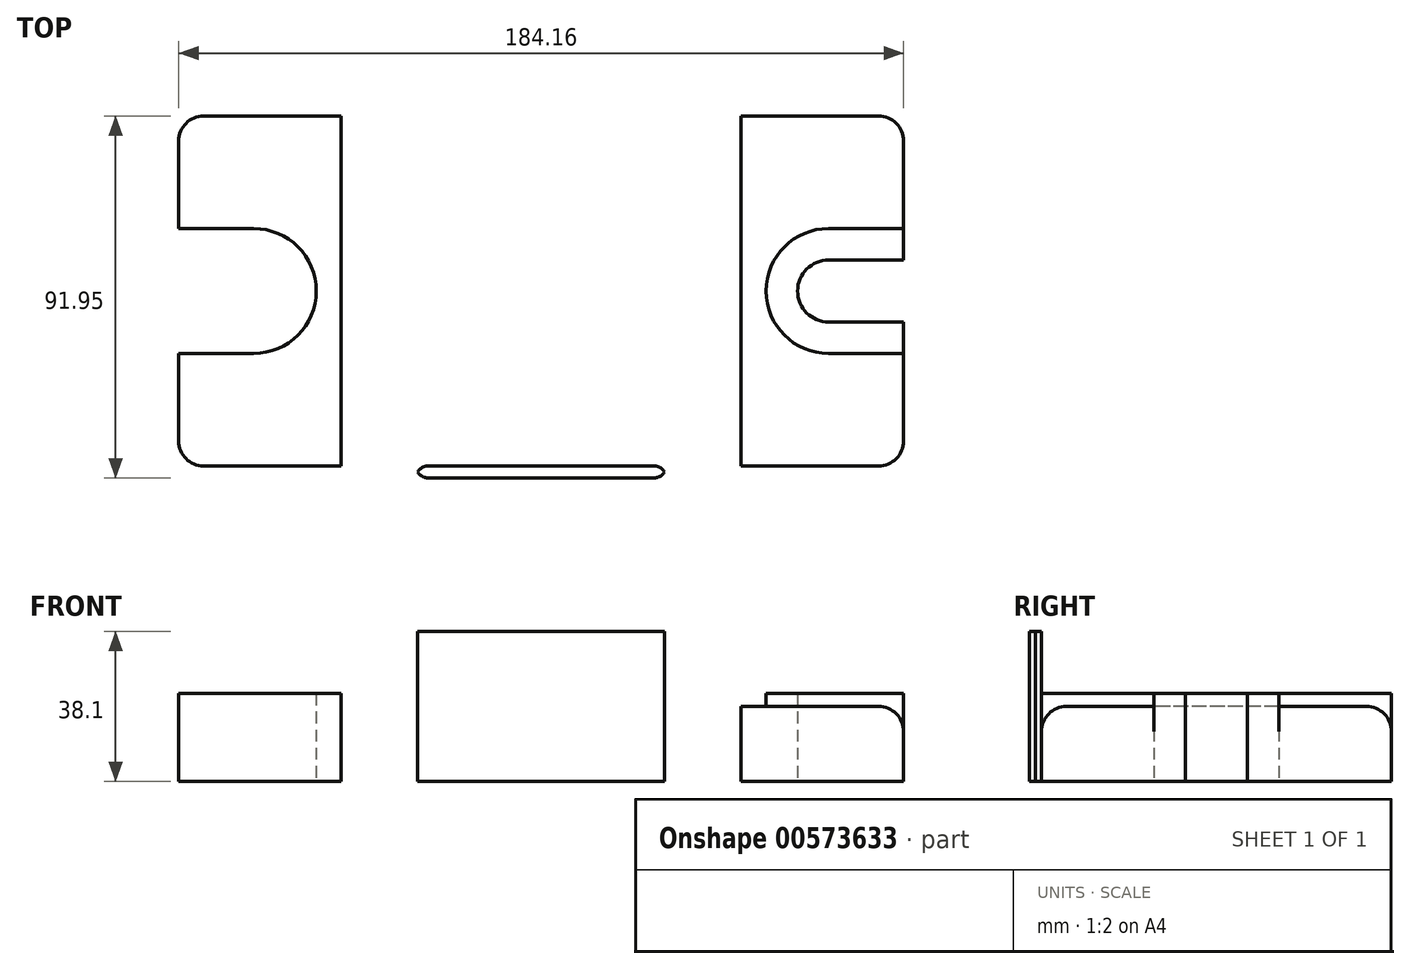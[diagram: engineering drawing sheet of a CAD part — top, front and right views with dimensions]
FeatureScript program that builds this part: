
annotation { "Feature Type Name" : "Feature", "Feature Type Description" : "" }
export const myFeature = defineFeature(function(context is Context, id is Id, definition is map)
    precondition{}
    {
        {
            var Q0;
            Q0=qCreatedBy(makeId("Top.planeOp"),FACE);
            var sketch = newSketch(context, id + "F0", { "sketchPlane" : qUnion([Q0])});
            skLineSegment(sketch, "E0.bottom", {"start": v(-92.08, 44.45) * mm, "end": v(92.08, 44.45) * mm});
            skLineSegment(sketch, "E0.top", {"start": v(-92.08, -44.45) * mm, "end": v(92.08, -44.45) * mm});
            skLineSegment(sketch, "E0.left", {"start": v(-92.08, 44.45) * mm, "end": v(-92.08, -44.45) * mm});
            skLineSegment(sketch, "E0.right", {"start": v(92.08, 44.45) * mm, "end": v(92.08, -44.45) * mm});
            skLineSegment(sketch, "E1.bottom", {"start": v(-50.8, 44.45) * mm, "end": v(50.8, 44.45) * mm});
            skLineSegment(sketch, "E1.top", {"start": v(-50.8, -44.45) * mm, "end": v(50.8, -44.45) * mm});
            skLineSegment(sketch, "E1.left", {"start": v(-50.8, 44.45) * mm, "end": v(-50.8, -44.45) * mm});
            skLineSegment(sketch, "E1.right", {"start": v(50.8, 44.45) * mm, "end": v(50.8, -44.45) * mm});
            skLineSegment(sketch, "E2", {"start": v(0, 44.45) * mm, "end": v(0, -44.45) * mm, "construction": true});
            skLineSegment(sketch, "E3", {"start": v(92.08, 0) * mm, "end": v(-92.08, 0) * mm, "construction": true});
            skPoint(sketch, "E4", {"position": v(0, 0) * mm});
            skLineSegment(sketch, "E5.0.startCap", {"start": v(73.03, 7.87) * mm, "end": v(73.03, 7.87) * mm});
            skLineSegment(sketch, "E6.MirrorCS", {"start": v(-73.03, 7.87) * mm, "end": v(-73.03, 7.87) * mm});
            skPoint(sketch, "E7", {"position": v(-31.75, -44.45) * mm});
            skLineSegment(sketch, "E8.top", {"start": v(-31.75, -47.5) * mm, "end": v(31.75, -47.5) * mm});
            skLineSegment(sketch, "E8.left", {"start": v(-31.75, -44.45) * mm, "end": v(-31.75, -47.5) * mm});
            skLineSegment(sketch, "E9", {"start": v(31.75, -47.5) * mm, "end": v(31.75, -44.45) * mm});
            skLineSegment(sketch, "E10", {"start": v(-92.07, 0) * mm, "end": v(-73.03, 0) * mm, "construction": true});
            skArc(sketch, "E11.0.startCap", {"start": v(-92.08, -15.88) * mm, "mid": v(-107.95, 0) * mm, "end": v(-92.08, 15.87) * mm});
            skArc(sketch, "E11.0.endCap", {"start": v(-73.03, 15.87) * mm, "mid": v(-57.15, 0) * mm, "end": v(-73.03, -15.88) * mm});
            skLineSegment(sketch, "E11.0.left", {"start": v(-92.08, 15.88) * mm, "end": v(-73.03, 15.88) * mm});
            skLineSegment(sketch, "E11.0.right", {"start": v(-92.08, -15.88) * mm, "end": v(-73.03, -15.88) * mm});
            skArc(sketch, "E12.0.startCap", {"start": v(-92.08, -7.87) * mm, "mid": v(-99.95, 0) * mm, "end": v(-92.08, 7.87) * mm});
            skArc(sketch, "E12.0.endCap", {"start": v(-73.03, 7.87) * mm, "mid": v(-65.15, 0) * mm, "end": v(-73.03, -7.87) * mm});
            skLineSegment(sketch, "E12.0.left", {"start": v(-92.08, 7.87) * mm, "end": v(-73.03, 7.87) * mm});
            skLineSegment(sketch, "E12.0.right", {"start": v(-92.08, -7.87) * mm, "end": v(-73.03, -7.87) * mm});
            skLineSegment(sketch, "E13.MirrorCS", {"start": v(92.08, 15.88) * mm, "end": v(73.03, 15.88) * mm});
            skArc(sketch, "E14.MirrorCS", {"start": v(73.03, 15.88) * mm, "mid": v(57.15, 0) * mm, "end": v(73.03, -15.87) * mm});
            skLineSegment(sketch, "E15.MirrorCS", {"start": v(92.08, 7.87) * mm, "end": v(73.03, 7.87) * mm});
            skArc(sketch, "E16.MirrorCS", {"start": v(73.03, 7.87) * mm, "mid": v(65.15, 0) * mm, "end": v(73.03, -7.87) * mm});
            skLineSegment(sketch, "E17.MirrorCS", {"start": v(92.08, -7.87) * mm, "end": v(73.03, -7.87) * mm});
            skLineSegment(sketch, "E18.MirrorCS", {"start": v(92.08, -15.87) * mm, "end": v(73.03, -15.87) * mm});
            skPoint(sketch, "E19", {"position": v(0, -47.5) * mm});
            skSolve(sketch);
        }
        {
            var Q0;
            {var subQ8=sQuery(id+"F0.wireOp",EDGE,"E1.left");Q0=makeQuery(id+"F0.imprint","IMPRINT",FACE,{"disambiguationData":[TD([[makeQuery(id+"F0.imprint","IMPRINT",EDGE,{"derivedFrom":subQ8}),-1.0]])]});}
            var Q1;
            {var subQ7=sQuery(id+"F0.wireOp",EDGE,"E1.right");Q1=makeQuery(id+"F0.imprint","IMPRINT",FACE,{"disambiguationData":[TD([[makeQuery(id+"F0.imprint","IMPRINT",EDGE,{"derivedFrom":subQ7}),1.0]])]});}
            var Q2;
            Q2=makeQuery(id+"F0.imprint","IMPRINT",FACE,{"disambiguationData":[TD([[makeQuery(id+"F0.imprint","IMPRINT",EDGE,{"derivedFrom":sQuery(id+"F0.wireOp",EDGE,"E1.bottom")}),-1.0]])]});
            var Q3;
            Q3=makeQuery(id+"F0.imprint","IMPRINT",FACE,{"disambiguationData":[TD([[makeQuery(id+"F0.imprint","IMPRINT",EDGE,{"derivedFrom":sQuery(id+"F0.wireOp",EDGE,"E8.top")}),1.0]])]});
            var Q4;
            Q4=makeQuery(id+"F0.imprint","IMPRINT",FACE,{"disambiguationData":[TD([[makeQuery(id+"F0.imprint","IMPRINT",EDGE,{"derivedFrom":sQuery(id+"F0.wireOp",EDGE,"E11.0.endCap")}),-1.0]])]});
            var Q5;
            {var subQ0=sQuery(id+"F0.wireOp",EDGE,"E13.MirrorCS");Q5=makeQuery(id+"F0.imprint","IMPRINT",FACE,{"disambiguationData":[TD([[makeQuery(id+"F0.imprint","IMPRINT",EDGE,{"derivedFrom":subQ0}),1.0]])]});}
            extrude(context, id + "F1", {"entities" : qUnion([Q0, Q1, Q2, Q3, Q4, Q5]), "depth" : 19.05 * mm, "offsetDistance" : 25.4 * mm});
        }
        {
            var Q0;
            Q0=makeQuery(id+"F0.imprint","IMPRINT",FACE,{"disambiguationData":[TD([[makeQuery(id+"F0.imprint","IMPRINT",EDGE,{"derivedFrom":sQuery(id+"F0.wireOp",EDGE,"E1.bottom")}),-1.0]])]});
            var Q1;
            Q1=makeQuery(id+"F0.imprint","IMPRINT",FACE,{"disambiguationData":[TD([[makeQuery(id+"F0.imprint","IMPRINT",EDGE,{"derivedFrom":sQuery(id+"F0.wireOp",EDGE,"E8.top")}),1.0]])]});
            extrude(context, id + "F2", {"entities" : qUnion([Q0, Q1]), "operationType" : NewBodyOperationType.ADD, "depth" : 38.1 * mm, "offsetDistance" : 25.4 * mm});
        }
        {
            var Q0;
            Q0=makeQuery(id+"F0.imprint","IMPRINT",FACE,{"disambiguationData":[TD([[makeQuery(id+"F0.imprint","IMPRINT",EDGE,{"derivedFrom":sQuery(id+"F0.wireOp",EDGE,"E11.0.endCap")}),-1.0]])]});
            var Q1;
            {var subQ0=sQuery(id+"F0.wireOp",EDGE,"E13.MirrorCS");Q1=makeQuery(id+"F0.imprint","IMPRINT",FACE,{"disambiguationData":[TD([[makeQuery(id+"F0.imprint","IMPRINT",EDGE,{"derivedFrom":subQ0}),1.0]])]});}
            extrude(context, id + "F3", {"entities" : qUnion([Q0, Q1]), "operationType" : NewBodyOperationType.ADD, "depth" : 22.35 * mm, "offsetDistance" : 25.4 * mm});
        }
        {
            var Q0;
            Q0=makeQuery(id+"F1.opExtrude","SWEPT_EDGE",EDGE,{"disambiguationData":[OSD([sQuery(id+"F0.wireOp",EDGE,"E0.top"),sQuery(id+"F0.wireOp",EDGE,"E0.right")])]});
            var Q1;
            {var subQ0=sQuery(id+"F0.wireOp",EDGE,"E0.right");Q1=makeQuery(id+"F1.opExtrude","CAP_EDGE",EDGE,{"disambiguationData":[OSD([subQ0]),TDD([makeQuery(id+"F0.imprint","IMPRINT",EDGE,{"disambiguationData":[TD([[makeQuery(id+"F0.imprint","INTERSECT",VERTEX,{"derivedFrom":[subQ0,sQuery(id+"F0.wireOp",EDGE,"E17.MirrorCS")]}),-1.0]])],"derivedFrom":subQ0}),makeQuery(id+"F0.imprint","IMPRINT",EDGE,{"disambiguationData":[TD([[makeQuery(id+"F0.imprint","INTERSECT",VERTEX,{"derivedFrom":[sQuery(id+"F0.wireOp",EDGE,"E0.top"),subQ0]}),1.0]])],"derivedFrom":subQ0})])],"isStart":false});}
            var Q2;
            {var subQ0=sQuery(id+"F0.wireOp",EDGE,"E1.top");var subQ1=sQuery(id+"F0.wireOp",EDGE,"E0.top");Q2=makeQuery(id+"F1.opExtrude","CAP_EDGE",EDGE,{"disambiguationData":[OSD([subQ1,subQ0]),TDD([makeQuery(id+"F0.imprint","IMPRINT",EDGE,{"disambiguationData":[TD([[makeQuery(id+"F0.imprint","INTERSECT",VERTEX,{"derivedFrom":[subQ1,sQuery(id+"F0.wireOp",EDGE,"E0.right")]}),1.0]])],"derivedFrom":subQ1}),makeQuery(id+"F0.imprint","IMPRINT",EDGE,{"disambiguationData":[TD([[makeQuery(id+"F0.imprint","INTERSECT",VERTEX,{"derivedFrom":[subQ0,sQuery(id+"F0.wireOp",EDGE,"E9")]}),-1.0]])],"derivedFrom":subQ0})])],"isStart":false});}
            var Q3;
            {var subQ0=sQuery(id+"F0.wireOp",EDGE,"E0.right");var subQ1=makeQuery(id+"F0.imprint","INTERSECT",VERTEX,{"derivedFrom":[subQ0,sQuery(id+"F0.wireOp",EDGE,"E13.MirrorCS")]});Q3=makeQuery(id+"F1.opExtrude","CAP_EDGE",EDGE,{"disambiguationData":[OSD([subQ0]),TDD([makeQuery(id+"F0.imprint","IMPRINT",EDGE,{"disambiguationData":[TD([[makeQuery(id+"F0.imprint","INTERSECT",VERTEX,{"derivedFrom":[sQuery(id+"F0.wireOp",EDGE,"E0.bottom"),subQ0]}),-1.0]])],"derivedFrom":subQ0}),makeQuery(id+"F0.imprint","IMPRINT",EDGE,{"disambiguationData":[TD([[subQ1,-1.0]])],"derivedFrom":subQ0})])],"isStart":false});}
            var Q4;
            {var subQ3=sQuery(id+"F0.wireOp",EDGE,"E0.bottom");var subQ4=sQuery(id+"F0.wireOp",EDGE,"E1.bottom");Q4=makeQuery(id+"F2.boolean.opBoolean","SPLIT",EDGE,{"disambiguationData":[TD([makeQuery(id+"F2.opExtrude","SWEPT_FACE",FACE,{"disambiguationData":[OSD([sQuery(id+"F0.wireOp",EDGE,"E1.right")])]})])],"derivedFrom":makeQuery(id+"F1.opExtrude","CAP_EDGE",EDGE,{"disambiguationData":[OSD([subQ3,subQ4])],"isStart":false})});}
            var Q5;
            Q5=makeQuery(id+"F1.opExtrude","SWEPT_EDGE",EDGE,{"disambiguationData":[OSD([sQuery(id+"F0.wireOp",EDGE,"E0.bottom"),sQuery(id+"F0.wireOp",EDGE,"E0.right")])]});
            var Q6;
            Q6=makeQuery(id+"F2.opExtrude","SWEPT_EDGE",EDGE,{"disambiguationData":[OSD([sQuery(id+"F0.wireOp",EDGE,"E0.bottom"),sQuery(id+"F0.wireOp",EDGE,"E1.bottom"),sQuery(id+"F0.wireOp",EDGE,"E1.right")])]});
            var Q7;
            Q7=makeQuery(id+"F2.boolean.opBoolean","INTERSECT",EDGE,{"derivedFrom":[makeQuery(id+"F1.opExtrude","CAP_FACE",FACE,{"disambiguationData":[OSD([sQuery(id+"F0.wireOp",EDGE,"E0.bottom"),sQuery(id+"F0.wireOp",EDGE,"E0.top"),sQuery(id+"F0.wireOp",EDGE,"E0.left"),sQuery(id+"F0.wireOp",EDGE,"E0.right"),sQuery(id+"F0.wireOp",EDGE,"E1.bottom"),sQuery(id+"F0.wireOp",EDGE,"E1.top"),sQuery(id+"F0.wireOp",EDGE,"E8.top"),sQuery(id+"F0.wireOp",EDGE,"E8.left"),sQuery(id+"F0.wireOp",EDGE,"E9"),sQuery(id+"F0.wireOp",EDGE,"E12.0.endCap"),sQuery(id+"F0.wireOp",EDGE,"E12.0.left"),sQuery(id+"F0.wireOp",EDGE,"E12.0.right"),sQuery(id+"F0.wireOp",EDGE,"E15.MirrorCS"),sQuery(id+"F0.wireOp",EDGE,"E16.MirrorCS"),sQuery(id+"F0.wireOp",EDGE,"E17.MirrorCS")])],"isStart":false}),makeQuery(id+"F2.opExtrude","SWEPT_FACE",FACE,{"disambiguationData":[OSD([sQuery(id+"F0.wireOp",EDGE,"E1.right")])]})]});
            var Q8;
            Q8=makeQuery(id+"F2.opExtrude","SWEPT_EDGE",EDGE,{"disambiguationData":[OSD([sQuery(id+"F0.wireOp",EDGE,"E0.bottom"),sQuery(id+"F0.wireOp",EDGE,"E1.bottom"),sQuery(id+"F0.wireOp",EDGE,"E1.left")])]});
            var Q9;
            Q9=makeQuery(id+"F2.boolean.opBoolean","INTERSECT",EDGE,{"derivedFrom":[makeQuery(id+"F1.opExtrude","CAP_FACE",FACE,{"disambiguationData":[OSD([sQuery(id+"F0.wireOp",EDGE,"E0.bottom"),sQuery(id+"F0.wireOp",EDGE,"E0.top"),sQuery(id+"F0.wireOp",EDGE,"E0.left"),sQuery(id+"F0.wireOp",EDGE,"E0.right"),sQuery(id+"F0.wireOp",EDGE,"E1.bottom"),sQuery(id+"F0.wireOp",EDGE,"E1.top"),sQuery(id+"F0.wireOp",EDGE,"E8.top"),sQuery(id+"F0.wireOp",EDGE,"E8.left"),sQuery(id+"F0.wireOp",EDGE,"E9"),sQuery(id+"F0.wireOp",EDGE,"E12.0.endCap"),sQuery(id+"F0.wireOp",EDGE,"E12.0.left"),sQuery(id+"F0.wireOp",EDGE,"E12.0.right"),sQuery(id+"F0.wireOp",EDGE,"E15.MirrorCS"),sQuery(id+"F0.wireOp",EDGE,"E16.MirrorCS"),sQuery(id+"F0.wireOp",EDGE,"E17.MirrorCS")])],"isStart":false}),makeQuery(id+"F2.opExtrude","SWEPT_FACE",FACE,{"disambiguationData":[OSD([sQuery(id+"F0.wireOp",EDGE,"E1.left")])]})]});
            var Q10;
            {var subQ0=sQuery(id+"F0.wireOp",EDGE,"E0.left");var subQ1=makeQuery(id+"F0.imprint","INTERSECT",VERTEX,{"derivedFrom":[subQ0,sQuery(id+"F0.wireOp",EDGE,"E11.0.startCap"),sQuery(id+"F0.wireOp",EDGE,"E11.0.left")]});Q10=makeQuery(id+"F1.opExtrude","CAP_EDGE",EDGE,{"disambiguationData":[OSD([subQ0]),TDD([makeQuery(id+"F0.imprint","IMPRINT",EDGE,{"disambiguationData":[TD([[makeQuery(id+"F0.imprint","INTERSECT",VERTEX,{"derivedFrom":[sQuery(id+"F0.wireOp",EDGE,"E0.bottom"),subQ0]}),-1.0]])],"derivedFrom":subQ0}),makeQuery(id+"F0.imprint","IMPRINT",EDGE,{"disambiguationData":[TD([[subQ1,-1.0]])],"derivedFrom":subQ0})])],"isStart":false});}
            var Q11;
            Q11=makeQuery(id+"F1.opExtrude","SWEPT_EDGE",EDGE,{"disambiguationData":[OSD([sQuery(id+"F0.wireOp",EDGE,"E0.bottom"),sQuery(id+"F0.wireOp",EDGE,"E0.left")])]});
            var Q12;
            Q12=makeQuery(id+"F1.opExtrude","SWEPT_EDGE",EDGE,{"disambiguationData":[OSD([sQuery(id+"F0.wireOp",EDGE,"E0.top"),sQuery(id+"F0.wireOp",EDGE,"E0.left")])]});
            var Q13;
            {var subQ0=sQuery(id+"F0.wireOp",EDGE,"E1.top");var subQ1=sQuery(id+"F0.wireOp",EDGE,"E0.top");Q13=makeQuery(id+"F1.opExtrude","CAP_EDGE",EDGE,{"disambiguationData":[OSD([subQ1,subQ0]),TDD([makeQuery(id+"F0.imprint","IMPRINT",EDGE,{"disambiguationData":[TD([[makeQuery(id+"F0.imprint","INTERSECT",VERTEX,{"derivedFrom":[subQ1,sQuery(id+"F0.wireOp",EDGE,"E0.left")]}),-1.0]])],"derivedFrom":subQ1}),makeQuery(id+"F0.imprint","IMPRINT",EDGE,{"disambiguationData":[TD([[makeQuery(id+"F0.imprint","INTERSECT",VERTEX,{"derivedFrom":[subQ0,sQuery(id+"F0.wireOp",EDGE,"E8.left")]}),1.0]])],"derivedFrom":subQ0})])],"isStart":false});}
            var Q14;
            {var subQ0=sQuery(id+"F0.wireOp",EDGE,"E0.left");var subQ1=makeQuery(id+"F0.imprint","INTERSECT",VERTEX,{"derivedFrom":[subQ0,sQuery(id+"F0.wireOp",EDGE,"E11.0.startCap"),sQuery(id+"F0.wireOp",EDGE,"E11.0.right")]});Q14=makeQuery(id+"F1.opExtrude","CAP_EDGE",EDGE,{"disambiguationData":[OSD([subQ0]),TDD([makeQuery(id+"F0.imprint","IMPRINT",EDGE,{"disambiguationData":[TD([[subQ1,1.0]])],"derivedFrom":subQ0}),makeQuery(id+"F0.imprint","IMPRINT",EDGE,{"disambiguationData":[TD([[makeQuery(id+"F0.imprint","INTERSECT",VERTEX,{"derivedFrom":[sQuery(id+"F0.wireOp",EDGE,"E0.top"),subQ0]}),1.0]])],"derivedFrom":subQ0})])],"isStart":false});}
            fillet(context, id + "F4", {"entities" : qUnion([Q0, Q1, Q2, Q3, Q4, Q5, Q6, Q7, Q8, Q9, Q10, Q11, Q12, Q13, Q14]), "radius" : 6.35 * mm, "tangentPropagation" : true, "allowEdgeOverflow" : false});
        }
        {
            var Q0;
            {var subQ0=sQuery(id+"F0.wireOp",EDGE,"E8.left");var subQ1=sQuery(id+"F0.wireOp",EDGE,"E1.top");Q0=makeQuery(id+"F2.boolean.opBoolean","MERGE",EDGE,{"derivedFrom":[makeQuery(id+"F1.opExtrude","SWEPT_EDGE",EDGE,{"disambiguationData":[OSD([subQ1,subQ0])]}),makeQuery(id+"F2.opExtrude","SWEPT_EDGE",EDGE,{"disambiguationData":[OSD([subQ1,subQ0])]})]});}
            var Q1;
            {var subQ0=sQuery(id+"F0.wireOp",EDGE,"E9");var subQ1=sQuery(id+"F0.wireOp",EDGE,"E1.top");Q1=makeQuery(id+"F2.boolean.opBoolean","MERGE",EDGE,{"derivedFrom":[makeQuery(id+"F1.opExtrude","SWEPT_EDGE",EDGE,{"disambiguationData":[OSD([subQ1,subQ0])]}),makeQuery(id+"F2.opExtrude","SWEPT_EDGE",EDGE,{"disambiguationData":[OSD([subQ1,subQ0])]})]});}
            var Q2;
            {var subQ0=sQuery(id+"F0.wireOp",EDGE,"E18.MirrorCS");var subQ1=sQuery(id+"F0.wireOp",EDGE,"E0.right");var subQ2=sQuery(id+"F0.wireOp",EDGE,"E0.top");var subQ5=sQuery(id+"F0.wireOp",EDGE,"E17.MirrorCS");var subQ7=sQuery(id+"F0.wireOp",EDGE,"E1.top");var subQ9=sQuery(id+"F0.wireOp",EDGE,"E9");var subQ11=sQuery(id+"F0.wireOp",EDGE,"E15.MirrorCS");var subQ12=sQuery(id+"F0.wireOp",EDGE,"E1.bottom");var subQ14=sQuery(id+"F0.wireOp",EDGE,"E0.bottom");var subQ15=sQuery(id+"F0.wireOp",EDGE,"E16.MirrorCS");Q2=makeQuery(id+"F3.boolean.opBoolean","INTERSECT",EDGE,{"derivedFrom":[makeQuery(id+"F2.boolean.opBoolean","SPLIT",FACE,{"disambiguationData":[TD([makeQuery(id+"F1.opExtrude","SWEPT_FACE",FACE,{"disambiguationData":[OSD([subQ11])]})])],"derivedFrom":makeQuery(id+"F1.opExtrude","CAP_FACE",FACE,{"disambiguationData":[OSD([subQ14,subQ2,sQuery(id+"F0.wireOp",EDGE,"E0.left"),subQ1,subQ12,subQ7,sQuery(id+"F0.wireOp",EDGE,"E8.top"),sQuery(id+"F0.wireOp",EDGE,"E8.left"),subQ9,sQuery(id+"F0.wireOp",EDGE,"E12.0.endCap"),sQuery(id+"F0.wireOp",EDGE,"E12.0.left"),sQuery(id+"F0.wireOp",EDGE,"E12.0.right"),subQ11,subQ15,subQ5])],"isStart":false})}),makeQuery(id+"F3.opExtrude","SWEPT_FACE",FACE,{"disambiguationData":[OSD([subQ0])]})]});}
            var Q3;
            {var subQ0=sQuery(id+"F0.wireOp",EDGE,"E11.0.right");var subQ1=sQuery(id+"F0.wireOp",EDGE,"E0.left");var subQ2=sQuery(id+"F0.wireOp",EDGE,"E0.top");var subQ6=sQuery(id+"F0.wireOp",EDGE,"E12.0.right");var subQ9=sQuery(id+"F0.wireOp",EDGE,"E12.0.left");var subQ10=sQuery(id+"F0.wireOp",EDGE,"E0.bottom");var subQ12=sQuery(id+"F0.wireOp",EDGE,"E1.top");var subQ14=sQuery(id+"F0.wireOp",EDGE,"E8.left");var subQ16=sQuery(id+"F0.wireOp",EDGE,"E1.bottom");var subQ17=sQuery(id+"F0.wireOp",EDGE,"E12.0.endCap");Q3=makeQuery(id+"F3.boolean.opBoolean","INTERSECT",EDGE,{"derivedFrom":[makeQuery(id+"F2.boolean.opBoolean","SPLIT",FACE,{"disambiguationData":[TD([makeQuery(id+"F1.opExtrude","SWEPT_FACE",FACE,{"disambiguationData":[OSD([subQ17])]})])],"derivedFrom":makeQuery(id+"F1.opExtrude","CAP_FACE",FACE,{"disambiguationData":[OSD([subQ10,subQ2,subQ1,sQuery(id+"F0.wireOp",EDGE,"E0.right"),subQ16,subQ12,sQuery(id+"F0.wireOp",EDGE,"E8.top"),subQ14,sQuery(id+"F0.wireOp",EDGE,"E9"),subQ17,subQ9,subQ6,sQuery(id+"F0.wireOp",EDGE,"E15.MirrorCS"),sQuery(id+"F0.wireOp",EDGE,"E16.MirrorCS"),sQuery(id+"F0.wireOp",EDGE,"E17.MirrorCS")])],"isStart":false})}),makeQuery(id+"F3.opExtrude","SWEPT_FACE",FACE,{"disambiguationData":[OSD([subQ0])]})]});}
            fillet(context, id + "F5", {"entities" : qUnion([Q0, Q1, Q2, Q3]), "radius" : 3.05 * mm, "tangentPropagation" : true, "allowEdgeOverflow" : false});
        }
    });
